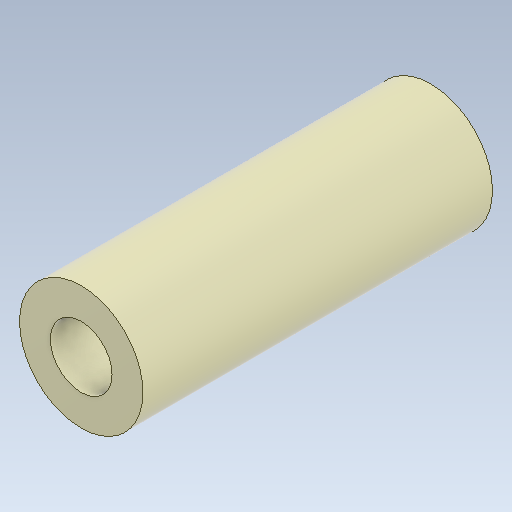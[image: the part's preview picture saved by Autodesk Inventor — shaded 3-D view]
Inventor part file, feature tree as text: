
AUTODESK INVENTOR PART (.ipt)
format: ipt  version: 2020.2 (Build 242310000, 310)  size: 106,496 bytes
history: native  units: mm
features: other x1, extrude x1, sketch x1
ambient origin geometry x8: Origin, YZ Plane, XZ Plane, XY Plane, X Axis, Y Axis, Z Axis, Center Point
bodies: Body1 (feature_tree)
feature tree (3):
  other  "ソリッド1"
  extrude  "押し出し1"  Depth=6.0mm
  sketch  "スケッチ1"
